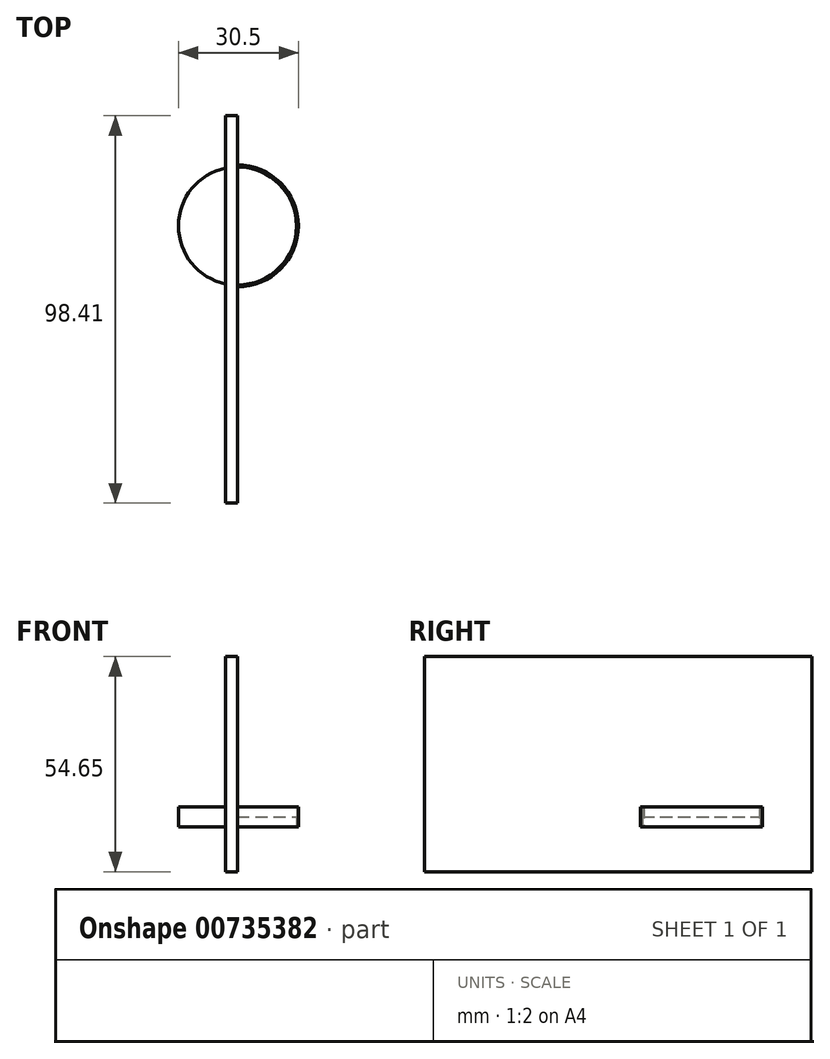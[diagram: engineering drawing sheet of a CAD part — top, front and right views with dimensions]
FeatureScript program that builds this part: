
annotation { "Feature Type Name" : "Feature", "Feature Type Description" : "" }
export const myFeature = defineFeature(function(context is Context, id is Id, definition is map)
    precondition{}
    {
        {
            var Q0;
            Q0=qCreatedBy(makeId("Top.planeOp"),FACE);
            var sketch = newSketch(context, id + "F0", { "sketchPlane" : qUnion([Q0])});
            skCircle(sketch, "E0", {"center": v(0, 0) * mm, "radius": 15.5 * mm});
            skCircle(sketch, "E1", {"center": v(0, 0) * mm, "radius": 15.15 * mm});
            skCircle(sketch, "E2", {"center": v(0, 0) * mm, "radius": 15 * mm});
            skLineSegment(sketch, "E3.bottom", {"start": v(0, 15.5) * mm, "end": v(37.46, 15.5) * mm});
            skLineSegment(sketch, "E3.top", {"start": v(0, -34.34) * mm, "end": v(37.46, -34.34) * mm});
            skLineSegment(sketch, "E3.left", {"start": v(0, 15.5) * mm, "end": v(0, -34.34) * mm});
            skLineSegment(sketch, "E3.right", {"start": v(37.46, 15.5) * mm, "end": v(37.46, -34.34) * mm});
            skSolve(sketch);
        }
        {
            var Q0;
            {var subQ0=sQuery(id+"F0.wireOp",EDGE,"E3.left");var subQ1=sQuery(id+"F0.wireOp",EDGE,"E2");var subQ2=makeQuery(id+"F0.imprint","INTERSECT",VERTEX,{"disambiguationData":[OD(0.0)],"derivedFrom":[subQ1,subQ0]});Q0=makeQuery(id+"F0.imprint","IMPRINT",FACE,{"disambiguationData":[TD([[makeQuery(id+"F0.imprint","IMPRINT",EDGE,{"disambiguationData":[TD([[subQ2,-1.0]])],"derivedFrom":subQ1}),1.0]])]});}
            extrude(context, id + "F1", {"entities" : qUnion([Q0]), "depth" : 2.54 * mm, "offsetDistance" : 25.4 * mm});
        }
        {
            var Q0;
            {var subQ0=sQuery(id+"F0.wireOp",EDGE,"E3.left");var subQ1=sQuery(id+"F0.wireOp",EDGE,"E1");var subQ2=makeQuery(id+"F0.imprint","INTERSECT",VERTEX,{"disambiguationData":[OD(0.0)],"derivedFrom":[subQ1,subQ0]});Q0=makeQuery(id+"F0.imprint","IMPRINT",FACE,{"disambiguationData":[TD([[makeQuery(id+"F0.imprint","IMPRINT",EDGE,{"disambiguationData":[TD([[subQ2,-1.0]])],"derivedFrom":subQ1}),1.0]])]});}
            var Q1;
            Q1=makeQuery(id+"F1.opExtrude","CAP_FACE",FACE,{"disambiguationData":[OSD([sQuery(id+"F0.wireOp",EDGE,"E2"),sQuery(id+"F0.wireOp",EDGE,"E3.left")])],"isStart":false});
            extrude(context, id + "F2", {"entities" : qUnion([Q0, Q1]), "operationType" : NewBodyOperationType.ADD, "depth" : 2.54 * mm, "offsetDistance" : 25.4 * mm});
        }
        {
            var Q0;
            {var subQ0=sQuery(id+"F0.wireOp",EDGE,"E3.left");var subQ4=sQuery(id+"F0.wireOp",EDGE,"E1");var subQ5=makeQuery(id+"F0.imprint","INTERSECT",VERTEX,{"disambiguationData":[OD(0.0)],"derivedFrom":[subQ4,subQ0]});Q0=makeQuery(id+"F0.imprint","IMPRINT",FACE,{"disambiguationData":[TD([[makeQuery(id+"F0.imprint","IMPRINT",EDGE,{"disambiguationData":[TD([[subQ5,-1.0]])],"derivedFrom":subQ4}),-1.0]])]});}
            extrude(context, id + "F3", {"entities" : qUnion([Q0]), "operationType" : NewBodyOperationType.ADD, "depth" : 5.08 * mm, "offsetDistance" : 25.4 * mm});
        }
        {
            var Q0;
            Q0=qCreatedBy(makeId("Right.planeOp"),FACE);
            var sketch = newSketch(context, id + "F4", { "sketchPlane" : qUnion([Q0])});
            skLineSegment(sketch, "E4.bottom", {"start": v(28, -11.44) * mm, "end": v(-70.42, -11.44) * mm});
            skLineSegment(sketch, "E4.top", {"start": v(28, 43.2) * mm, "end": v(-70.42, 43.2) * mm});
            skLineSegment(sketch, "E4.left", {"start": v(28, -11.44) * mm, "end": v(28, 43.2) * mm});
            skLineSegment(sketch, "E4.right", {"start": v(-70.42, -11.44) * mm, "end": v(-70.42, 43.2) * mm});
            skLineSegment(sketch, "E5", {"start": v(15.55, 0) * mm, "end": v(15.55, -11.44) * mm});
            skSolve(sketch);
        }
        {
            var Q0;
            Q0=makeQuery(id+"F4.imprint","IMPRINT",FACE,{"disambiguationData":[TD([[makeQuery(id+"F4.imprint","IMPRINT",EDGE,{"derivedFrom":sQuery(id+"F4.wireOp",EDGE,"E4.top")}),1.0]])]});
            extrude(context, id + "F5", {"entities" : qUnion([Q0]), "operationType" : NewBodyOperationType.ADD, "oppositeDirection" : true, "depth" : 3 * mm, "offsetDistance" : 25 * mm});
        }
    });
